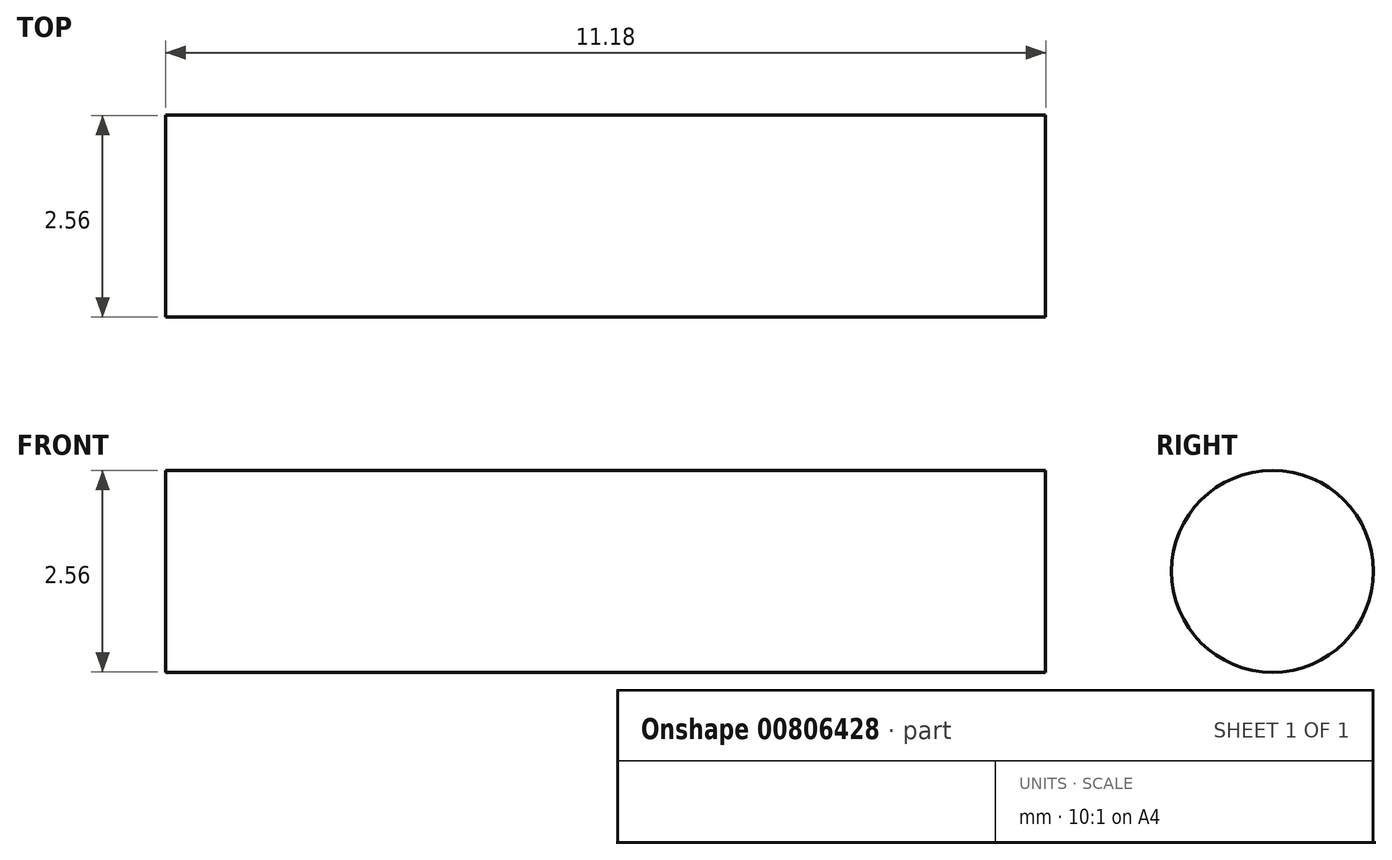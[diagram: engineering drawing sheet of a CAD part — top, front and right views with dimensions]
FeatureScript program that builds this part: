
annotation { "Feature Type Name" : "Feature", "Feature Type Description" : "" }
export const myFeature = defineFeature(function(context is Context, id is Id, definition is map)
    precondition{}
    {
        {
            var Q0;
            Q0=qCreatedBy(makeId("Right.planeOp"),FACE);
            var sketch = newSketch(context, id + "F0", { "sketchPlane" : qUnion([Q0])});
            skCircle(sketch, "E0", {"center": v(25.57, 36.03) * mm, "radius": 1.28 * mm});
            skPoint(sketch, "E0.first.point", {"position": v(26.84, 35.85) * mm});
            skPoint(sketch, "E0.second.point", {"position": v(25.23, 37.27) * mm});
            skPoint(sketch, "E0.third.point", {"position": v(25.26, 34.78) * mm});
            skSolve(sketch);
        }
        {
            var Q0;
            Q0 = qSketchRegion(id + "F0", true);
            extrude(context, id + "F1", {"entities" : qUnion([Q0]), "endBound" : BoundingType.SYMMETRIC, "depth" : 11.18 * mm, "offsetDistance" : 25.4 * mm});
        }
    });
